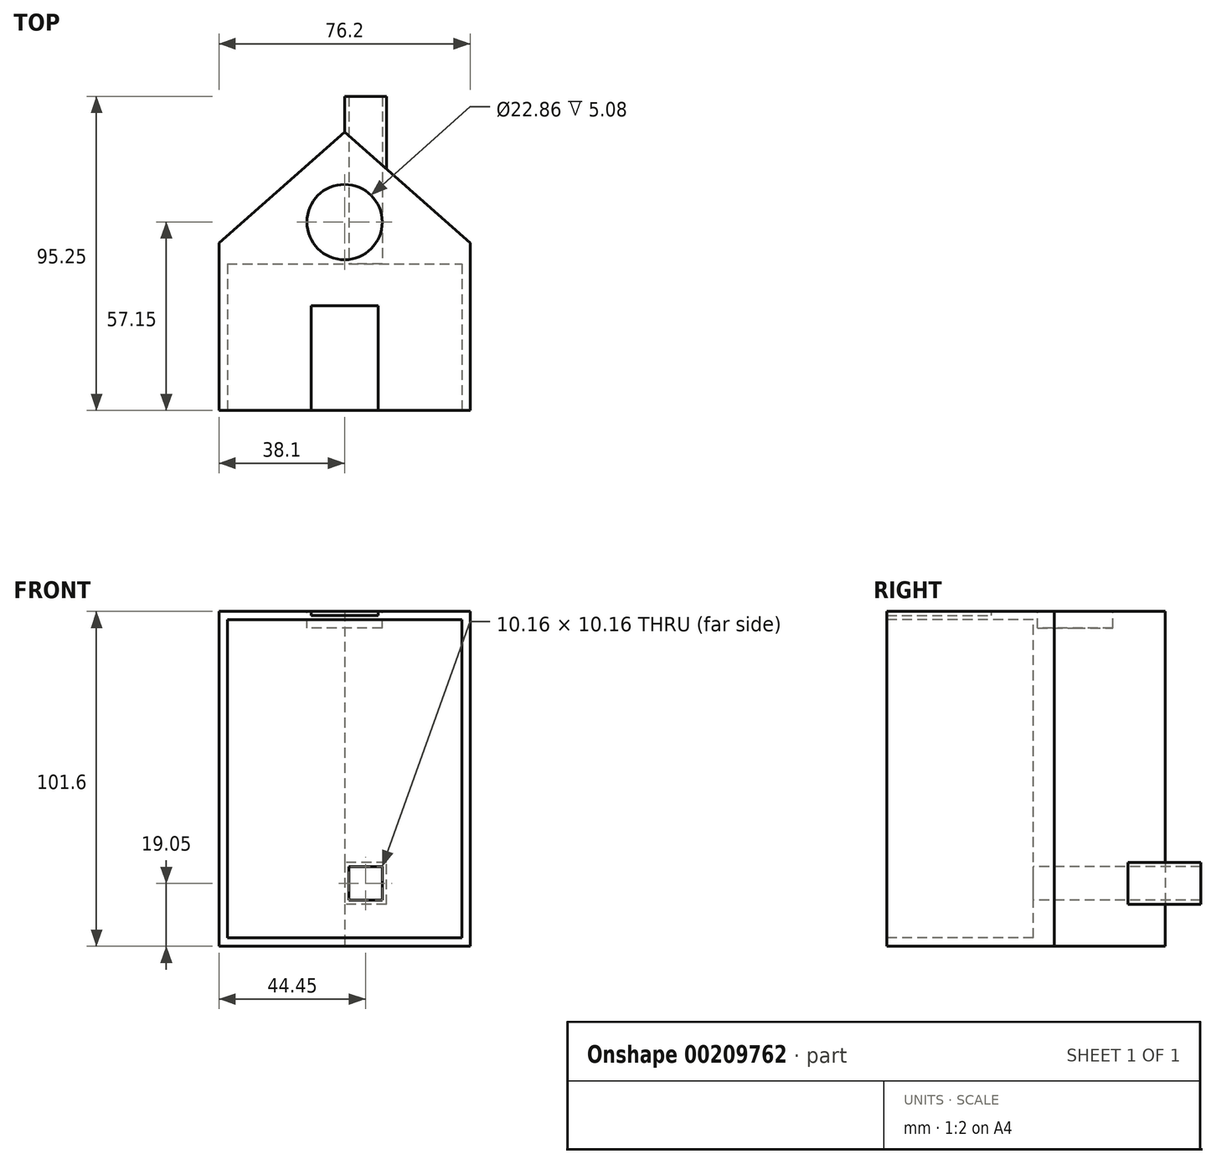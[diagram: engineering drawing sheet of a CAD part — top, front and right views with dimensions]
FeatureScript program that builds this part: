
annotation { "Feature Type Name" : "Feature", "Feature Type Description" : "" }
export const myFeature = defineFeature(function(context is Context, id is Id, definition is map)
    precondition{}
    {
        {
            var Q0;
            Q0=qCreatedBy(makeId("Top.planeOp"),FACE);
            var sketch = newSketch(context, id + "F0", { "sketchPlane" : qUnion([Q0])});
            skLineSegment(sketch, "E0.bottom", {"start": v(0, 0) * mm, "end": v(76.2, 0) * mm});
            skLineSegment(sketch, "E0.top", {"start": v(0, 50.8) * mm, "end": v(76.2, 50.8) * mm});
            skLineSegment(sketch, "E0.left", {"start": v(0, 0) * mm, "end": v(0, 50.8) * mm});
            skLineSegment(sketch, "E0.right", {"start": v(76.2, 0) * mm, "end": v(76.2, 50.8) * mm});
            skLineSegment(sketch, "E1", {"start": v(0, 50.8) * mm, "end": v(38.1, 84.4) * mm});
            skLineSegment(sketch, "E2", {"start": v(38.1, 84.4) * mm, "end": v(76.2, 50.8) * mm});
            skLineSegment(sketch, "E3.bottom", {"start": v(-101.6, 0) * mm, "end": v(-177.8, 0) * mm});
            skLineSegment(sketch, "E3.top", {"start": v(-101.6, 50.8) * mm, "end": v(-177.8, 50.8) * mm});
            skLineSegment(sketch, "E3.left", {"start": v(-101.6, 0) * mm, "end": v(-101.6, 50.8) * mm});
            skLineSegment(sketch, "E3.right", {"start": v(-177.8, 0) * mm, "end": v(-177.8, 50.8) * mm});
            skLineSegment(sketch, "E4.bottom", {"start": v(152.4, 0) * mm, "end": v(158.75, 0) * mm});
            skLineSegment(sketch, "E4.top", {"start": v(152.4, 50.8) * mm, "end": v(158.75, 50.8) * mm});
            skLineSegment(sketch, "E4.left", {"start": v(152.4, 0) * mm, "end": v(152.4, 50.8) * mm});
            skLineSegment(sketch, "E4.right", {"start": v(158.75, 0) * mm, "end": v(158.75, 50.8) * mm});
            skSolve(sketch);
        }
        {
            var Q0;
            Q0=makeQuery(id+"F0.imprint","IMPRINT",FACE,{"disambiguationData":[TD([[makeQuery(id+"F0.imprint","IMPRINT",EDGE,{"derivedFrom":sQuery(id+"F0.wireOp",EDGE,"E0.top")}),1.0]])]});
            var Q1;
            Q1=makeQuery(id+"F0.imprint","IMPRINT",FACE,{"disambiguationData":[TD([[makeQuery(id+"F0.imprint","IMPRINT",EDGE,{"derivedFrom":sQuery(id+"F0.wireOp",EDGE,"E0.bottom")}),1.0]])]});
            extrude(context, id + "F1", {"entities" : qUnion([Q0, Q1]), "depth" : 101.6 * mm});
        }
        {
            var Q0;
            Q0=makeQuery(id+"F1.opExtrude","CAP_FACE",FACE,{"disambiguationData":[OSD([sQuery(id+"F0.wireOp",EDGE,"E0.bottom"),sQuery(id+"F0.wireOp",EDGE,"E0.left"),sQuery(id+"F0.wireOp",EDGE,"E0.right"),sQuery(id+"F0.wireOp",EDGE,"E1"),sQuery(id+"F0.wireOp",EDGE,"E2")])],"isStart":false});
            var sketch = newSketch(context, id + "F2", { "sketchPlane" : qUnion([Q0])});
            skLineSegment(sketch, "E5.bottom", {"start": v(48.26, 0) * mm, "end": v(27.94, 0) * mm});
            skLineSegment(sketch, "E5.top", {"start": v(48.26, 31.75) * mm, "end": v(27.94, 31.75) * mm});
            skLineSegment(sketch, "E5.left", {"start": v(48.26, 0) * mm, "end": v(48.26, 31.75) * mm});
            skLineSegment(sketch, "E5.right", {"start": v(27.94, 0) * mm, "end": v(27.94, 31.75) * mm});
            skCircle(sketch, "E6", {"center": v(38.1, 57.15) * mm, "radius": 11.43 * mm});
            skSolve(sketch);
        }
        {
            var Q0;
            Q0=makeQuery(id+"F1.opExtrude","SWEPT_FACE",FACE,{"disambiguationData":[OSD([sQuery(id+"F0.wireOp",EDGE,"E0.bottom")])]});
            var sketch = newSketch(context, id + "F3", { "sketchPlane" : qUnion([Q0])});
            skLineSegment(sketch, "E7.bottom", {"start": v(2.54, 2.54) * mm, "end": v(73.66, 2.54) * mm});
            skLineSegment(sketch, "E7.top", {"start": v(2.54, 99.06) * mm, "end": v(73.66, 99.06) * mm});
            skLineSegment(sketch, "E7.left", {"start": v(2.54, 2.54) * mm, "end": v(2.54, 99.06) * mm});
            skLineSegment(sketch, "E7.right", {"start": v(73.66, 2.54) * mm, "end": v(73.66, 99.06) * mm});
            skSolve(sketch);
        }
        {
            var Q0;
            Q0 = qSketchRegion(id + "F3", true);
            extrude(context, id + "F4", {"entities" : qUnion([Q0]), "operationType" : NewBodyOperationType.REMOVE, "oppositeDirection" : true, "depth" : 44.45 * mm});
        }
        {
            var Q0;
            Q0=makeQuery(id+"F2.imprint","IMPRINT",FACE,{"disambiguationData":[TD([[makeQuery(id+"F2.imprint","IMPRINT",EDGE,{"derivedFrom":sQuery(id+"F2.wireOp",EDGE,"E6")}),1.0]])]});
            extrude(context, id + "F5", {"entities" : qUnion([Q0]), "operationType" : NewBodyOperationType.REMOVE, "oppositeDirection" : true, "depth" : 5.08 * mm});
        }
        {
            var Q0;
            Q0 = qSketchRegion(id + "F2", true);
            extrude(context, id + "F6", {"entities" : qUnion([Q0]), "operationType" : NewBodyOperationType.REMOVE, "oppositeDirection" : true, "depth" : 1.27 * mm});
        }
        {
            var Q0;
            Q0=makeQuery(id+"F4.boolean.opBoolean","COPY",FACE,{"derivedFrom":makeQuery(id+"F4.opExtrude","CAP_FACE",FACE,{"disambiguationData":[OSD([sQuery(id+"F3.wireOp",EDGE,"E7.bottom"),sQuery(id+"F3.wireOp",EDGE,"E7.top"),sQuery(id+"F3.wireOp",EDGE,"E7.left"),sQuery(id+"F3.wireOp",EDGE,"E7.right")])],"isStart":false})});
            var sketch = newSketch(context, id + "F7", { "sketchPlane" : qUnion([Q0])});
            skLineSegment(sketch, "E8.bottom", {"start": v(38.1, 25.4) * mm, "end": v(50.8, 25.4) * mm});
            skLineSegment(sketch, "E8.top", {"start": v(38.1, 12.7) * mm, "end": v(50.8, 12.7) * mm});
            skLineSegment(sketch, "E8.left", {"start": v(38.1, 25.4) * mm, "end": v(38.1, 12.7) * mm});
            skLineSegment(sketch, "E8.right", {"start": v(50.8, 25.4) * mm, "end": v(50.8, 12.7) * mm});
            skLineSegment(sketch, "E9.bottom", {"start": v(49.53, 13.97) * mm, "end": v(39.37, 13.97) * mm});
            skLineSegment(sketch, "E9.top", {"start": v(49.53, 24.13) * mm, "end": v(39.37, 24.13) * mm});
            skLineSegment(sketch, "E9.left", {"start": v(49.53, 13.97) * mm, "end": v(49.53, 24.13) * mm});
            skLineSegment(sketch, "E9.right", {"start": v(39.37, 13.97) * mm, "end": v(39.37, 24.13) * mm});
            skSolve(sketch);
        }
        {
            var Q0;
            Q0 = qSketchRegion(id + "F7", true);
            extrude(context, id + "F8", {"entities" : qUnion([Q0]), "operationType" : NewBodyOperationType.ADD, "oppositeDirection" : true, "depth" : 50.8 * mm});
        }
        {
            var Q0;
            Q0=makeQuery(id+"F7.imprint","IMPRINT",FACE,{"disambiguationData":[TD([[makeQuery(id+"F7.imprint","IMPRINT",EDGE,{"derivedFrom":sQuery(id+"F7.wireOp",EDGE,"E9.bottom")}),-1.0]])]});
            extrude(context, id + "F9", {"entities" : qUnion([Q0]), "operationType" : NewBodyOperationType.REMOVE, "endBound" : BoundingType.THROUGH_ALL, "oppositeDirection" : true, "depth" : 25.4 * mm});
        }
    });
